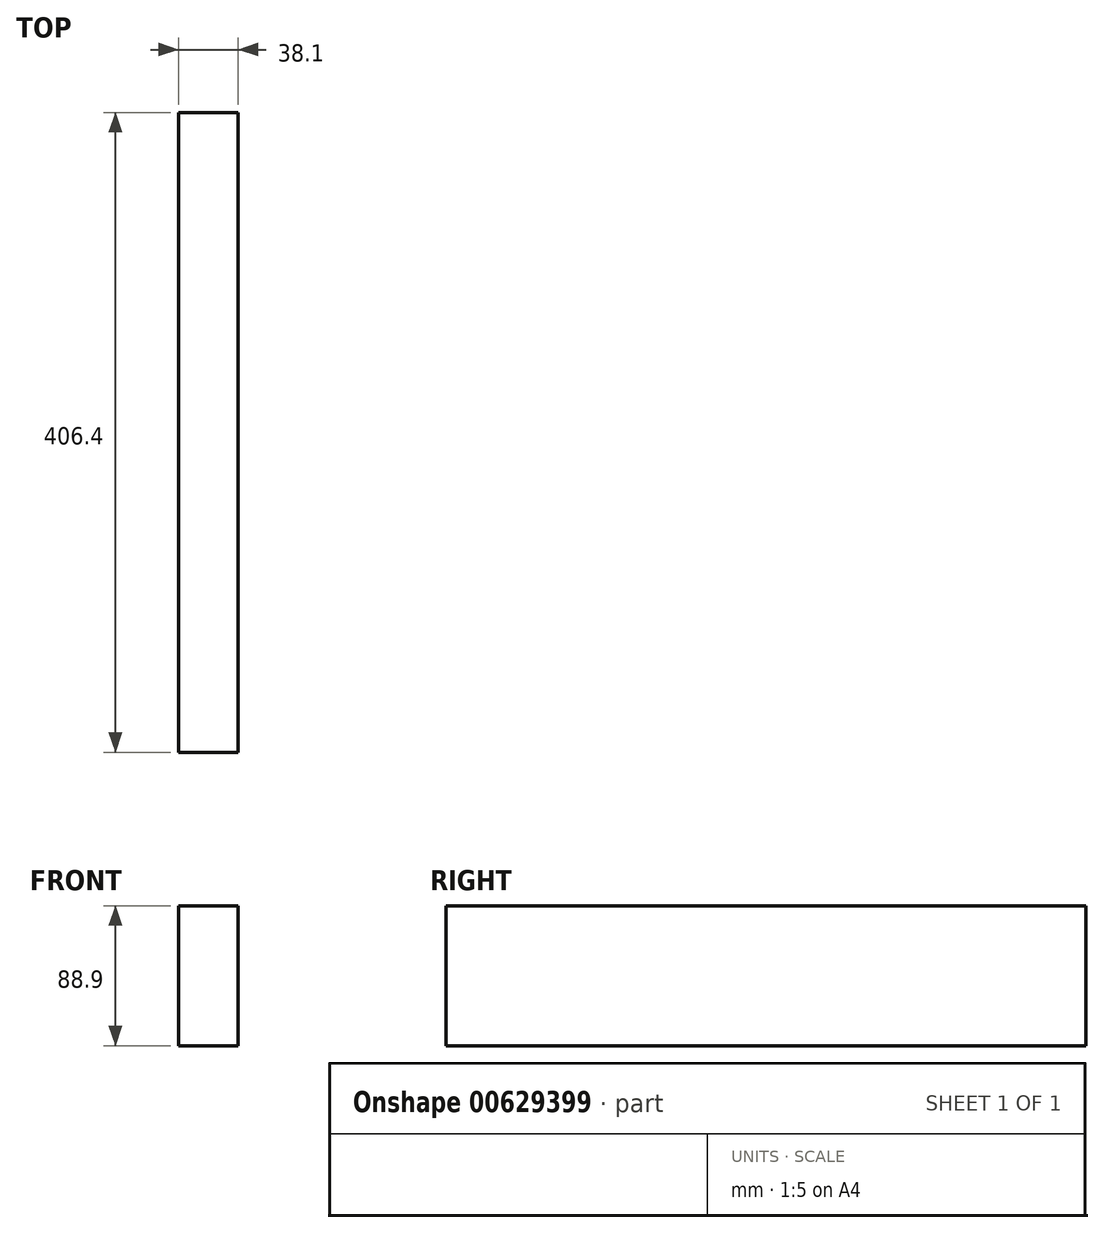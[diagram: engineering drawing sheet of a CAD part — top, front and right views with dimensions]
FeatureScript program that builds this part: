
annotation { "Feature Type Name" : "Feature", "Feature Type Description" : "" }
export const myFeature = defineFeature(function(context is Context, id is Id, definition is map)
    precondition{}
    {
        {
            var Q0;
            Q0=qCreatedBy(makeId("Front.planeOp"),FACE);
            var sketch = newSketch(context, id + "F0", { "sketchPlane" : qUnion([Q0])});
            skLineSegment(sketch, "E0.bottom", {"start": v(-16.29, 88.9) * mm, "end": v(21.81, 88.9) * mm});
            skLineSegment(sketch, "E0.top", {"start": v(-16.29, 0) * mm, "end": v(21.81, 0) * mm});
            skLineSegment(sketch, "E0.left", {"start": v(-16.29, 88.9) * mm, "end": v(-16.29, 0) * mm});
            skLineSegment(sketch, "E0.right", {"start": v(21.81, 88.9) * mm, "end": v(21.81, 0) * mm});
            skSolve(sketch);
        }
        {
            var Q0;
            Q0=qSketchRegion(id+"F0",true);
            var Q1;
            Q1=makeQuery(id+"F0.imprint","IMPRINT",FACE,{"disambiguationData":[TD([[makeQuery(id+"F0.imprint","IMPRINT",EDGE,{"derivedFrom":sQuery(id+"F0.wireOp",EDGE,"E0.bottom")}),-1.0]])]});
            extrude(context, id + "F1", {"entities" : qUnion([Q0, Q1]), "depth" : 406.4 * mm, "offsetDistance" : 25.4 * mm});
        }
    });
